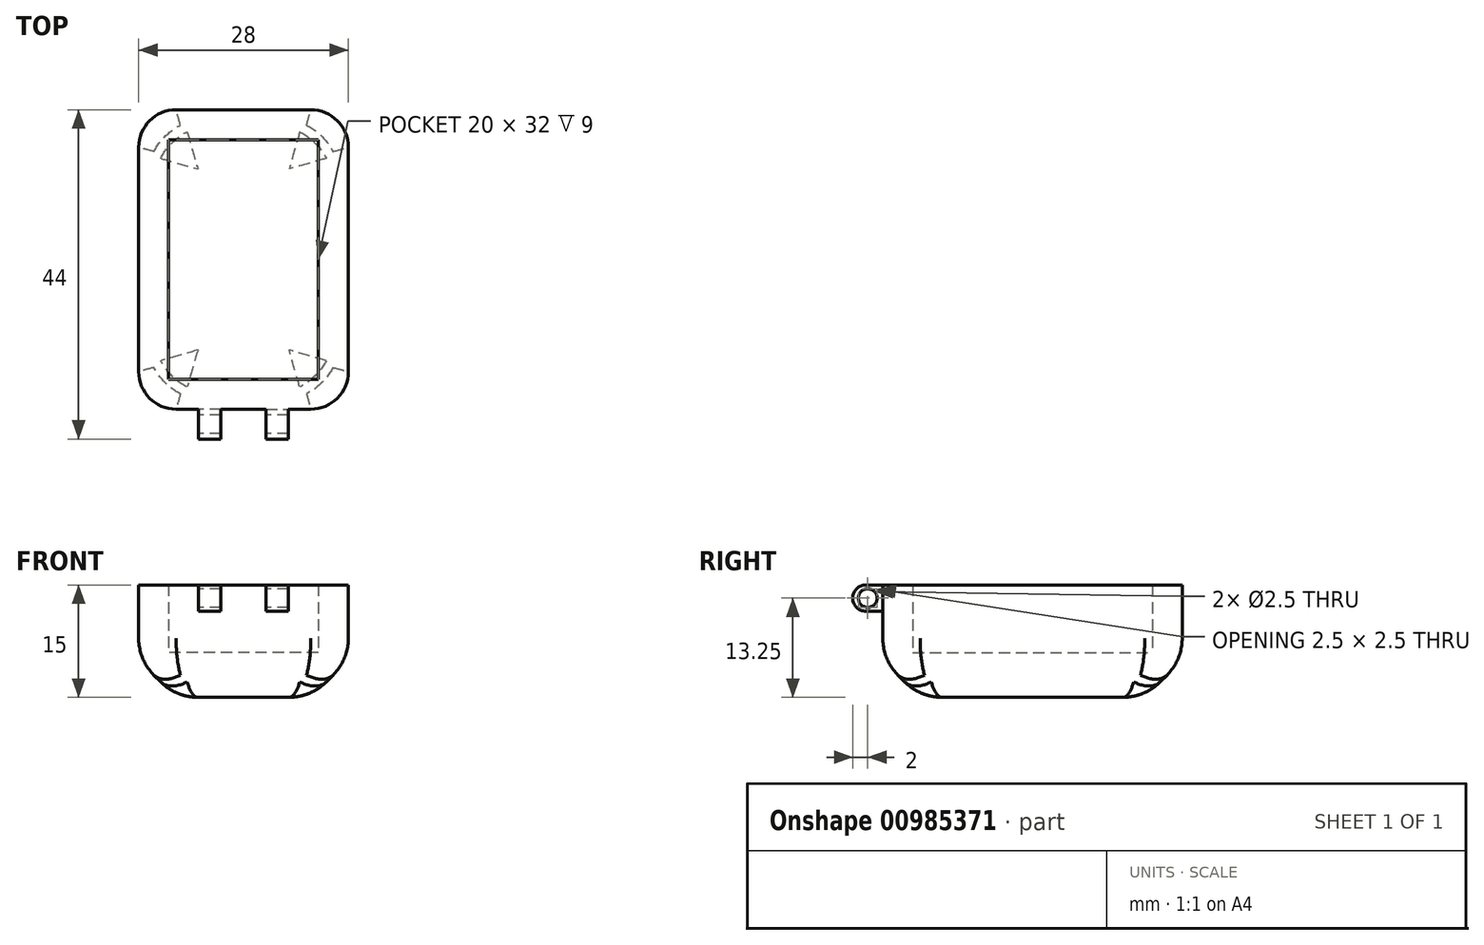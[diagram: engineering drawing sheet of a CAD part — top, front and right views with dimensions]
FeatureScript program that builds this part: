
annotation { "Feature Type Name" : "Feature", "Feature Type Description" : "" }
export const myFeature = defineFeature(function(context is Context, id is Id, definition is map)
    precondition{}
    {
        {
            var Q0;
            Q0=qCreatedBy(makeId("Top.planeOp"),FACE);
            var sketch = newSketch(context, id + "F0", { "sketchPlane" : qUnion([Q0])});
            skLineSegment(sketch, "E0.bottom", {"start": v(10, -16) * mm, "end": v(-10, -16) * mm});
            skLineSegment(sketch, "E0.top", {"start": v(10, 16) * mm, "end": v(-10, 16) * mm});
            skLineSegment(sketch, "E0.left", {"start": v(10, -16) * mm, "end": v(10, 16) * mm});
            skLineSegment(sketch, "E0.right", {"start": v(-10, -16) * mm, "end": v(-10, 16) * mm});
            skPoint(sketch, "E0.middle", {"position": v(0, 0) * mm});
            skLineSegment(sketch, "E1.bottom", {"start": v(14, -20) * mm, "end": v(-14, -20) * mm});
            skLineSegment(sketch, "E1.top", {"start": v(14, 20) * mm, "end": v(-14, 20) * mm});
            skLineSegment(sketch, "E1.left", {"start": v(14, -20) * mm, "end": v(14, 20) * mm});
            skLineSegment(sketch, "E1.right", {"start": v(-14, -20) * mm, "end": v(-14, 20) * mm});
            skSolve(sketch);
        }
        {
            var Q0;
            Q0=makeQuery(id+"F0.imprint","IMPRINT",FACE,{"disambiguationData":[TD([[makeQuery(id+"F0.imprint","IMPRINT",EDGE,{"derivedFrom":sQuery(id+"F0.wireOp",EDGE,"E0.bottom")}),1.0]])]});
            extrude(context, id + "F1", {"entities" : qUnion([Q0]), "depth" : 15 * mm, "offsetDistance" : 25 * mm});
        }
        {
            var Q0;
            Q0=makeQuery(id+"F0.imprint","IMPRINT",FACE,{"disambiguationData":[TD([[makeQuery(id+"F0.imprint","IMPRINT",EDGE,{"derivedFrom":sQuery(id+"F0.wireOp",EDGE,"E0.bottom")}),-1.0]])]});
            extrude(context, id + "F2", {"entities" : qUnion([Q0]), "operationType" : NewBodyOperationType.ADD, "depth" : 6 * mm, "offsetDistance" : 25 * mm});
        }
        {
            var Q0;
            Q0=makeQuery(id+"F1.opExtrude","CAP_EDGE",EDGE,{"disambiguationData":[OSD([sQuery(id+"F0.wireOp",EDGE,"E1.right")])],"isStart":true});
            var Q1;
            Q1=makeQuery(id+"F1.opExtrude","CAP_EDGE",EDGE,{"disambiguationData":[OSD([sQuery(id+"F0.wireOp",EDGE,"E1.bottom")])],"isStart":true});
            var Q2;
            Q2=makeQuery(id+"F1.opExtrude","CAP_EDGE",EDGE,{"disambiguationData":[OSD([sQuery(id+"F0.wireOp",EDGE,"E1.left")])],"isStart":true});
            var Q3;
            Q3=makeQuery(id+"F1.opExtrude","CAP_EDGE",EDGE,{"disambiguationData":[OSD([sQuery(id+"F0.wireOp",EDGE,"E1.top")])],"isStart":true});
            chamfer(context, id + "F3", {"entities" : qUnion([Q0, Q1, Q2, Q3]), "width" : 5 * mm, "tangentPropagation" : true});
        }
        {
            var Q0;
            {var subQ0=sQuery(id+"F0.wireOp",EDGE,"E0.right");var subQ1=sQuery(id+"F0.wireOp",EDGE,"E0.left");var subQ2=sQuery(id+"F0.wireOp",EDGE,"E0.top");var subQ3=sQuery(id+"F0.wireOp",EDGE,"E0.bottom");var subQ4=sQuery(id+"F0.wireOp",EDGE,"E1.right");Q0=makeQuery(id+"F3.opChamfer","BLEND_EDGE",EDGE,{"blendedFrom":[makeQuery(id+"F1.opExtrude","CAP_EDGE",EDGE,{"disambiguationData":[OSD([subQ4])],"isStart":true}),makeQuery(id+"F2.boolean.opBoolean","MERGE",FACE,{"derivedFrom":[makeQuery(id+"F1.opExtrude","CAP_FACE",FACE,{"disambiguationData":[OSD([subQ3,subQ2,subQ1,subQ0,sQuery(id+"F0.wireOp",EDGE,"E1.bottom"),sQuery(id+"F0.wireOp",EDGE,"E1.top"),sQuery(id+"F0.wireOp",EDGE,"E1.left"),subQ4])],"isStart":true}),makeQuery(id+"F2.opExtrude","CAP_FACE",FACE,{"disambiguationData":[OSD([subQ3,subQ2,subQ1,subQ0])],"isStart":true})]})],"blendedInto":[makeQuery(id+"F2.boolean.opBoolean","MERGE",FACE,{"derivedFrom":[makeQuery(id+"F1.opExtrude","CAP_FACE",FACE,{"disambiguationData":[OSD([subQ3,subQ2,subQ1,subQ0,sQuery(id+"F0.wireOp",EDGE,"E1.bottom"),sQuery(id+"F0.wireOp",EDGE,"E1.top"),sQuery(id+"F0.wireOp",EDGE,"E1.left"),subQ4])],"isStart":true}),makeQuery(id+"F2.opExtrude","CAP_FACE",FACE,{"disambiguationData":[OSD([subQ3,subQ2,subQ1,subQ0])],"isStart":true})]})]});}
            var Q1;
            {var subQ0=sQuery(id+"F0.wireOp",EDGE,"E0.right");var subQ1=sQuery(id+"F0.wireOp",EDGE,"E0.left");var subQ2=sQuery(id+"F0.wireOp",EDGE,"E0.top");var subQ3=sQuery(id+"F0.wireOp",EDGE,"E0.bottom");var subQ4=sQuery(id+"F0.wireOp",EDGE,"E1.bottom");Q1=makeQuery(id+"F3.opChamfer","BLEND_EDGE",EDGE,{"blendedFrom":[makeQuery(id+"F1.opExtrude","CAP_EDGE",EDGE,{"disambiguationData":[OSD([subQ4])],"isStart":true}),makeQuery(id+"F2.boolean.opBoolean","MERGE",FACE,{"derivedFrom":[makeQuery(id+"F1.opExtrude","CAP_FACE",FACE,{"disambiguationData":[OSD([subQ3,subQ2,subQ1,subQ0,subQ4,sQuery(id+"F0.wireOp",EDGE,"E1.top"),sQuery(id+"F0.wireOp",EDGE,"E1.left"),sQuery(id+"F0.wireOp",EDGE,"E1.right")])],"isStart":true}),makeQuery(id+"F2.opExtrude","CAP_FACE",FACE,{"disambiguationData":[OSD([subQ3,subQ2,subQ1,subQ0])],"isStart":true})]})],"blendedInto":[makeQuery(id+"F2.boolean.opBoolean","MERGE",FACE,{"derivedFrom":[makeQuery(id+"F1.opExtrude","CAP_FACE",FACE,{"disambiguationData":[OSD([subQ3,subQ2,subQ1,subQ0,subQ4,sQuery(id+"F0.wireOp",EDGE,"E1.top"),sQuery(id+"F0.wireOp",EDGE,"E1.left"),sQuery(id+"F0.wireOp",EDGE,"E1.right")])],"isStart":true}),makeQuery(id+"F2.opExtrude","CAP_FACE",FACE,{"disambiguationData":[OSD([subQ3,subQ2,subQ1,subQ0])],"isStart":true})]})]});}
            var Q2;
            {var subQ0=sQuery(id+"F0.wireOp",EDGE,"E0.right");var subQ1=sQuery(id+"F0.wireOp",EDGE,"E0.left");var subQ2=sQuery(id+"F0.wireOp",EDGE,"E0.top");var subQ3=sQuery(id+"F0.wireOp",EDGE,"E0.bottom");var subQ4=sQuery(id+"F0.wireOp",EDGE,"E1.left");Q2=makeQuery(id+"F3.opChamfer","BLEND_EDGE",EDGE,{"blendedFrom":[makeQuery(id+"F1.opExtrude","CAP_EDGE",EDGE,{"disambiguationData":[OSD([subQ4])],"isStart":true}),makeQuery(id+"F2.boolean.opBoolean","MERGE",FACE,{"derivedFrom":[makeQuery(id+"F1.opExtrude","CAP_FACE",FACE,{"disambiguationData":[OSD([subQ3,subQ2,subQ1,subQ0,sQuery(id+"F0.wireOp",EDGE,"E1.bottom"),sQuery(id+"F0.wireOp",EDGE,"E1.top"),subQ4,sQuery(id+"F0.wireOp",EDGE,"E1.right")])],"isStart":true}),makeQuery(id+"F2.opExtrude","CAP_FACE",FACE,{"disambiguationData":[OSD([subQ3,subQ2,subQ1,subQ0])],"isStart":true})]})],"blendedInto":[makeQuery(id+"F2.boolean.opBoolean","MERGE",FACE,{"derivedFrom":[makeQuery(id+"F1.opExtrude","CAP_FACE",FACE,{"disambiguationData":[OSD([subQ3,subQ2,subQ1,subQ0,sQuery(id+"F0.wireOp",EDGE,"E1.bottom"),sQuery(id+"F0.wireOp",EDGE,"E1.top"),subQ4,sQuery(id+"F0.wireOp",EDGE,"E1.right")])],"isStart":true}),makeQuery(id+"F2.opExtrude","CAP_FACE",FACE,{"disambiguationData":[OSD([subQ3,subQ2,subQ1,subQ0])],"isStart":true})]})]});}
            var Q3;
            {var subQ0=sQuery(id+"F0.wireOp",EDGE,"E0.right");var subQ1=sQuery(id+"F0.wireOp",EDGE,"E0.left");var subQ2=sQuery(id+"F0.wireOp",EDGE,"E0.top");var subQ3=sQuery(id+"F0.wireOp",EDGE,"E0.bottom");var subQ4=sQuery(id+"F0.wireOp",EDGE,"E1.top");Q3=makeQuery(id+"F3.opChamfer","BLEND_EDGE",EDGE,{"blendedFrom":[makeQuery(id+"F1.opExtrude","CAP_EDGE",EDGE,{"disambiguationData":[OSD([subQ4])],"isStart":true}),makeQuery(id+"F2.boolean.opBoolean","MERGE",FACE,{"derivedFrom":[makeQuery(id+"F1.opExtrude","CAP_FACE",FACE,{"disambiguationData":[OSD([subQ3,subQ2,subQ1,subQ0,sQuery(id+"F0.wireOp",EDGE,"E1.bottom"),subQ4,sQuery(id+"F0.wireOp",EDGE,"E1.left"),sQuery(id+"F0.wireOp",EDGE,"E1.right")])],"isStart":true}),makeQuery(id+"F2.opExtrude","CAP_FACE",FACE,{"disambiguationData":[OSD([subQ3,subQ2,subQ1,subQ0])],"isStart":true})]})],"blendedInto":[makeQuery(id+"F2.boolean.opBoolean","MERGE",FACE,{"derivedFrom":[makeQuery(id+"F1.opExtrude","CAP_FACE",FACE,{"disambiguationData":[OSD([subQ3,subQ2,subQ1,subQ0,sQuery(id+"F0.wireOp",EDGE,"E1.bottom"),subQ4,sQuery(id+"F0.wireOp",EDGE,"E1.left"),sQuery(id+"F0.wireOp",EDGE,"E1.right")])],"isStart":true}),makeQuery(id+"F2.opExtrude","CAP_FACE",FACE,{"disambiguationData":[OSD([subQ3,subQ2,subQ1,subQ0])],"isStart":true})]})]});}
            var Q4;
            {var subQ0=sQuery(id+"F0.wireOp",EDGE,"E1.right");Q4=makeQuery(id+"F3.opChamfer","BLEND_EDGE",EDGE,{"blendedFrom":[makeQuery(id+"F1.opExtrude","CAP_EDGE",EDGE,{"disambiguationData":[OSD([subQ0])],"isStart":true}),makeQuery(id+"F1.opExtrude","SWEPT_FACE",FACE,{"disambiguationData":[OSD([subQ0])]})],"blendedInto":[makeQuery(id+"F1.opExtrude","SWEPT_FACE",FACE,{"disambiguationData":[OSD([subQ0])]})]});}
            var Q5;
            {var subQ0=sQuery(id+"F0.wireOp",EDGE,"E1.bottom");Q5=makeQuery(id+"F3.opChamfer","BLEND_EDGE",EDGE,{"blendedFrom":[makeQuery(id+"F1.opExtrude","CAP_EDGE",EDGE,{"disambiguationData":[OSD([subQ0])],"isStart":true}),makeQuery(id+"F1.opExtrude","SWEPT_FACE",FACE,{"disambiguationData":[OSD([subQ0])]})],"blendedInto":[makeQuery(id+"F1.opExtrude","SWEPT_FACE",FACE,{"disambiguationData":[OSD([subQ0])]})]});}
            var Q6;
            {var subQ0=sQuery(id+"F0.wireOp",EDGE,"E1.left");Q6=makeQuery(id+"F3.opChamfer","BLEND_EDGE",EDGE,{"blendedFrom":[makeQuery(id+"F1.opExtrude","CAP_EDGE",EDGE,{"disambiguationData":[OSD([subQ0])],"isStart":true}),makeQuery(id+"F1.opExtrude","SWEPT_FACE",FACE,{"disambiguationData":[OSD([subQ0])]})],"blendedInto":[makeQuery(id+"F1.opExtrude","SWEPT_FACE",FACE,{"disambiguationData":[OSD([subQ0])]})]});}
            var Q7;
            {var subQ0=sQuery(id+"F0.wireOp",EDGE,"E1.top");Q7=makeQuery(id+"F3.opChamfer","BLEND_EDGE",EDGE,{"blendedFrom":[makeQuery(id+"F1.opExtrude","CAP_EDGE",EDGE,{"disambiguationData":[OSD([subQ0])],"isStart":true}),makeQuery(id+"F1.opExtrude","SWEPT_FACE",FACE,{"disambiguationData":[OSD([subQ0])]})],"blendedInto":[makeQuery(id+"F1.opExtrude","SWEPT_FACE",FACE,{"disambiguationData":[OSD([subQ0])]})]});}
            fillet(context, id + "F4", {"entities" : qUnion([Q0, Q1, Q2, Q3, Q4, Q5, Q6, Q7]), "radius" : 7 * mm, "tangentPropagation" : true, "allowEdgeOverflow" : false});
        }
        {
            var Q0;
            Q0=makeQuery(id+"F1.opExtrude","SWEPT_EDGE",EDGE,{"disambiguationData":[OSD([sQuery(id+"F0.wireOp",EDGE,"E1.bottom"),sQuery(id+"F0.wireOp",EDGE,"E1.left")])]});
            var Q1;
            Q1=makeQuery(id+"F1.opExtrude","SWEPT_EDGE",EDGE,{"disambiguationData":[OSD([sQuery(id+"F0.wireOp",EDGE,"E1.bottom"),sQuery(id+"F0.wireOp",EDGE,"E1.right")])]});
            var Q2;
            Q2=makeQuery(id+"F1.opExtrude","SWEPT_EDGE",EDGE,{"disambiguationData":[OSD([sQuery(id+"F0.wireOp",EDGE,"E1.top"),sQuery(id+"F0.wireOp",EDGE,"E1.right")])]});
            var Q3;
            Q3=makeQuery(id+"F1.opExtrude","SWEPT_EDGE",EDGE,{"disambiguationData":[OSD([sQuery(id+"F0.wireOp",EDGE,"E1.top"),sQuery(id+"F0.wireOp",EDGE,"E1.left")])]});
            fillet(context, id + "F5", {"entities" : qUnion([Q0, Q1, Q2, Q3]), "radius" : 5 * mm, "tangentPropagation" : true, "allowEdgeOverflow" : false});
        }
        {
            var Q0;
            Q0=makeQuery(id+"F1.opExtrude","SWEPT_FACE",FACE,{"disambiguationData":[OSD([sQuery(id+"F0.wireOp",EDGE,"E1.bottom")])]});
            var sketch = newSketch(context, id + "F6", { "sketchPlane" : qUnion([Q0])});
            skLineSegment(sketch, "E2.bottom", {"start": v(6, 11.5) * mm, "end": v(-6, 11.5) * mm});
            skLineSegment(sketch, "E2.top", {"start": v(6, 15) * mm, "end": v(-6, 15) * mm});
            skLineSegment(sketch, "E2.left", {"start": v(6, 11.5) * mm, "end": v(6, 15) * mm});
            skLineSegment(sketch, "E2.right", {"start": v(-6, 11.5) * mm, "end": v(-6, 15) * mm});
            skPoint(sketch, "E2.middle", {"position": v(0, 13.25) * mm});
            skLineSegment(sketch, "E3", {"start": v(-3, 15) * mm, "end": v(-3, 11.5) * mm});
            skLineSegment(sketch, "E4", {"start": v(3, 15) * mm, "end": v(3, 11.5) * mm});
            skSolve(sketch);
        }
        {
            var Q0;
            {var subQ0=sQuery(id+"F6.wireOp",EDGE,"E2.right");Q0=makeQuery(id+"F6.imprint","IMPRINT",FACE,{"disambiguationData":[TD([[makeQuery(id+"F6.imprint","IMPRINT",EDGE,{"derivedFrom":subQ0}),-1.0]])]});}
            var Q1;
            {var subQ0=sQuery(id+"F6.wireOp",EDGE,"E2.left");Q1=makeQuery(id+"F6.imprint","IMPRINT",FACE,{"disambiguationData":[TD([[makeQuery(id+"F6.imprint","IMPRINT",EDGE,{"derivedFrom":subQ0}),1.0]])]});}
            extrude(context, id + "F7", {"entities" : qUnion([Q0, Q1]), "operationType" : NewBodyOperationType.ADD, "depth" : 4 * mm, "offsetDistance" : 25 * mm});
        }
        {
            var Q0;
            {var subQ0=sQuery(id+"F6.wireOp",EDGE,"E2.bottom");Q0=makeQuery(id+"F7.opExtrude","CAP_EDGE",EDGE,{"disambiguationData":[OSD([subQ0]),TDD([makeQuery(id+"F6.imprint","IMPRINT",EDGE,{"disambiguationData":[TD([[makeQuery(id+"F6.imprint","INTERSECT",VERTEX,{"derivedFrom":[subQ0,sQuery(id+"F6.wireOp",EDGE,"E2.right")]}),1.0]])],"derivedFrom":subQ0})])],"isStart":false});}
            var Q1;
            {var subQ0=sQuery(id+"F6.wireOp",EDGE,"E2.top");Q1=makeQuery(id+"F7.opExtrude","CAP_EDGE",EDGE,{"disambiguationData":[OSD([subQ0]),TDD([makeQuery(id+"F6.imprint","IMPRINT",EDGE,{"disambiguationData":[TD([[makeQuery(id+"F6.imprint","INTERSECT",VERTEX,{"derivedFrom":[subQ0,sQuery(id+"F6.wireOp",EDGE,"E3")]}),-1.0]])],"derivedFrom":subQ0})])],"isStart":false});}
            var Q2;
            {var subQ0=sQuery(id+"F6.wireOp",EDGE,"E2.bottom");Q2=makeQuery(id+"F7.opExtrude","CAP_EDGE",EDGE,{"disambiguationData":[OSD([subQ0]),TDD([makeQuery(id+"F6.imprint","IMPRINT",EDGE,{"disambiguationData":[TD([[makeQuery(id+"F6.imprint","INTERSECT",VERTEX,{"derivedFrom":[subQ0,sQuery(id+"F6.wireOp",EDGE,"E2.left")]}),-1.0]])],"derivedFrom":subQ0})])],"isStart":false});}
            var Q3;
            {var subQ0=sQuery(id+"F6.wireOp",EDGE,"E2.top");Q3=makeQuery(id+"F7.opExtrude","CAP_EDGE",EDGE,{"disambiguationData":[OSD([subQ0]),TDD([makeQuery(id+"F6.imprint","IMPRINT",EDGE,{"disambiguationData":[TD([[makeQuery(id+"F6.imprint","INTERSECT",VERTEX,{"derivedFrom":[subQ0,sQuery(id+"F6.wireOp",EDGE,"E4")]}),1.0]])],"derivedFrom":subQ0})])],"isStart":false});}
            fillet(context, id + "F8", {"entities" : qUnion([Q0, Q1, Q2, Q3]), "radius" : 1.75 * mm, "tangentPropagation" : true, "allowEdgeOverflow" : false});
        }
        {
            var Q0;
            Q0=makeQuery(id+"F7.opExtrude","SWEPT_FACE",FACE,{"disambiguationData":[OSD([sQuery(id+"F6.wireOp",EDGE,"E2.right")])]});
            var sketch = newSketch(context, id + "F9", { "sketchPlane" : qUnion([Q0])});
            skCircle(sketch, "E5", {"center": v(22, 13.25) * mm, "radius": 1.25 * mm});
            skSolve(sketch);
        }
        {
            var Q0;
            Q0=makeQuery(id+"F9.imprint","IMPRINT",FACE,{"disambiguationData":[TD([[makeQuery(id+"F9.imprint","IMPRINT",EDGE,{"derivedFrom":sQuery(id+"F9.wireOp",EDGE,"E5")}),1.0]])]});
            extrude(context, id + "F10", {"entities" : qUnion([Q0]), "operationType" : NewBodyOperationType.REMOVE, "oppositeDirection" : true, "depth" : 25 * mm, "offsetDistance" : 25 * mm});
        }
    });
